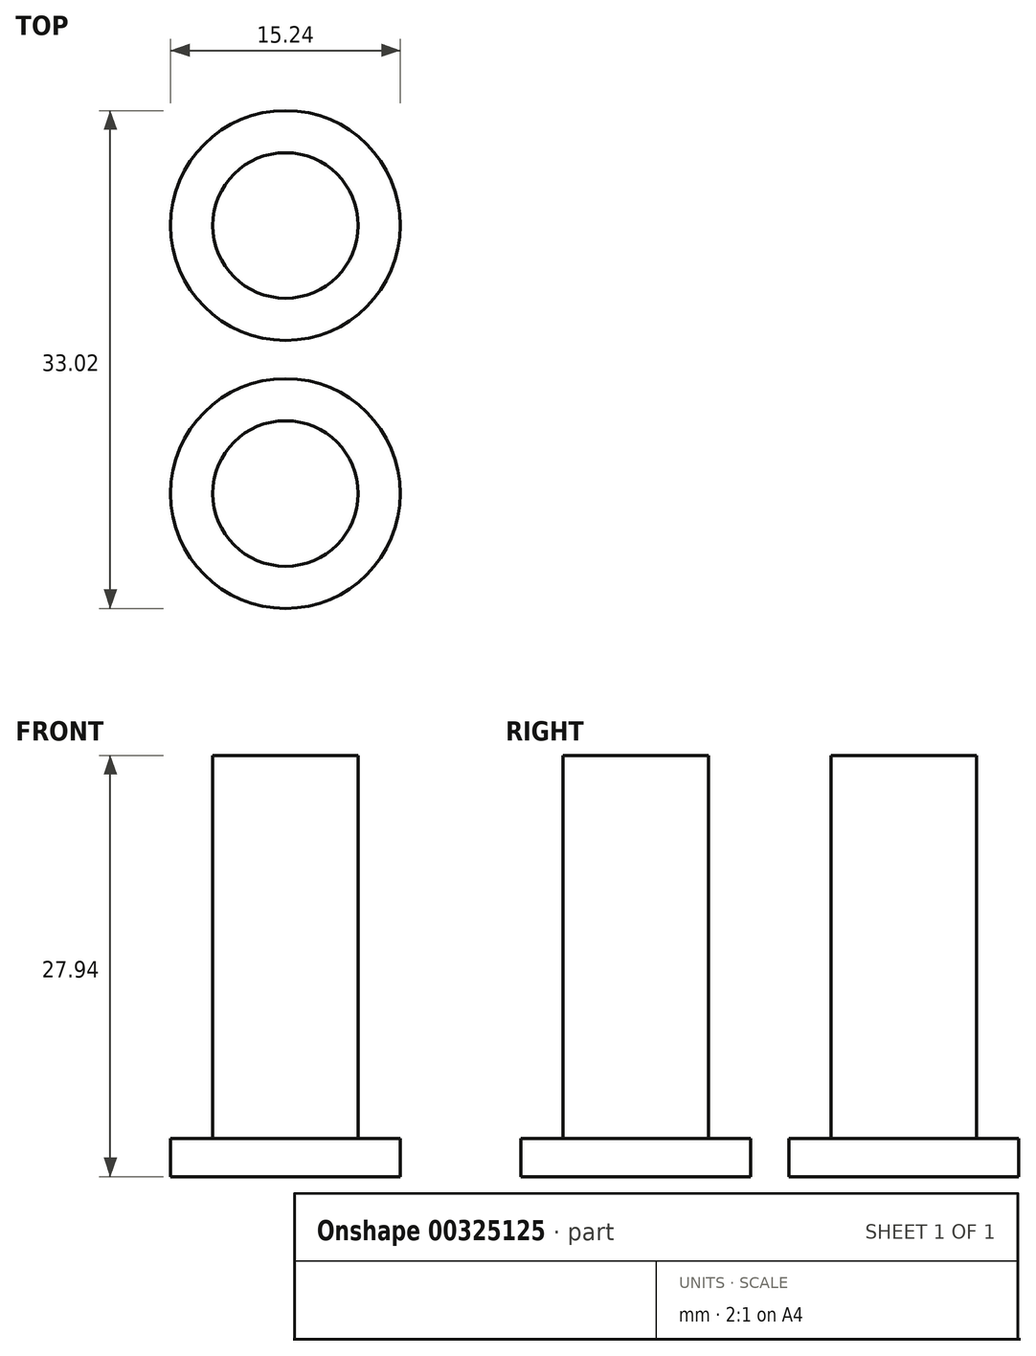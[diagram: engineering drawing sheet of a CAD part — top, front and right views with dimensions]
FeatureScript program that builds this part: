
annotation { "Feature Type Name" : "Feature", "Feature Type Description" : "" }
export const myFeature = defineFeature(function(context is Context, id is Id, definition is map)
    precondition{}
    {
        {
            var Q0;
            Q0=qCreatedBy(makeId("Top.planeOp"),FACE);
            var sketch = newSketch(context, id + "F0", { "sketchPlane" : qUnion([Q0])});
            skCircle(sketch, "E0", {"center": v(0, 0) * mm, "radius": 4.83 * mm});
            skSolve(sketch);
        }
        {
            var Q0;
            Q0=makeQuery(id+"F0.imprint","IMPRINT",FACE,{"disambiguationData":[TD([[makeQuery(id+"F0.imprint","IMPRINT",EDGE,{"derivedFrom":sQuery(id+"F0.wireOp",EDGE,"E0")}),1.0]])]});
            extrude(context, id + "F1", {"entities" : qUnion([Q0]), "depth" : 25.4 * mm});
        }
        {
            var Q0;
            Q0=makeQuery(id+"F1.opExtrude","CAP_FACE",FACE,{"disambiguationData":[OSD([sQuery(id+"F0.wireOp",EDGE,"E0")])],"isStart":false});
            var sketch = newSketch(context, id + "F2", { "sketchPlane" : qUnion([Q0])});
            skCircle(sketch, "E1", {"center": v(0, 0) * mm, "radius": 7.62 * mm});
            skSolve(sketch);
        }
        {
            var Q0;
            Q0=makeQuery(id+"F2.imprint","IMPRINT",FACE,{"disambiguationData":[TD([[makeQuery(id+"F2.imprint","IMPRINT",EDGE,{"derivedFrom":sQuery(id+"F2.wireOp",EDGE,"E1")}),1.0]])]});
            var Q1;
            Q1=makeQuery(id+"F2.imprint","IMPRINT",FACE,{"disambiguationData":[TD([[makeQuery(id+"F2.imprint","IMPRINT",EDGE,{"derivedFrom":makeQuery(id+"F1.opExtrude","CAP_EDGE",EDGE,{"disambiguationData":[OSD([sQuery(id+"F0.wireOp",EDGE,"E0")])],"isStart":false})}),1.0]])]});
            extrude(context, id + "F3", {"entities" : qUnion([Q0, Q1]), "operationType" : NewBodyOperationType.ADD, "depth" : 2.54 * mm});
        }
        {
            var Q0;
            Q0=makeQuery(id+"F1.opExtrude","SWEPT_BODY",BODY,{"disambiguationData":[OSD([sQuery(id+"F0.wireOp",EDGE,"E0")])]});
            transform(context, id + "F4", {"entities" : qUnion([Q0]), "transformType" : TransformType.COPY});
        }
        {
            var Q0;
            Q0=makeQuery(id+"F1.opExtrude","SWEPT_BODY",BODY,{"disambiguationData":[OSD([sQuery(id+"F0.wireOp",EDGE,"E0")])]});
            transform(context, id + "F5", {"entities" : qUnion([Q0]), "transformType" : TransformType.TRANSLATION_3D, "dx" : 0 * mm, "dy" : 17.78 * mm, "dz" : 0 * mm, "makeCopy" : false});
        }
        {
            var Q0;
            Q0=qCreatedBy(makeId("Top.planeOp"),FACE);
            var sketch = newSketch(context, id + "F6", { "sketchPlane" : qUnion([Q0])});
            skLineSegment(sketch, "E2", {"start": v(0, 0) * mm, "end": v(18.45, 0) * mm});
            skSolve(sketch);
        }
        {
            var Q0;
            Q0=makeQuery(id+"F1.opExtrude","SWEPT_BODY",BODY,{"disambiguationData":[OSD([sQuery(id+"F0.wireOp",EDGE,"E0")])]});
            var Q1;
            Q1=makeQuery(id+"F4.opPattern","COPY",BODY,{"derivedFrom":makeQuery(id+"F1.opExtrude","SWEPT_BODY",BODY,{"disambiguationData":[OSD([sQuery(id+"F0.wireOp",EDGE,"E0")])]}),"instanceName":"1"});
            var Q2;
            Q2=sQuery(id+"F6.wireOp",EDGE,"E2");
            transform(context, id + "F7", {"entities" : qUnion([Q0, Q1]), "transformType" : TransformType.ROTATION, "transformAxis" : qUnion([Q2]), "angle" : 180 * degree, "makeCopy" : false});
        }
    });
